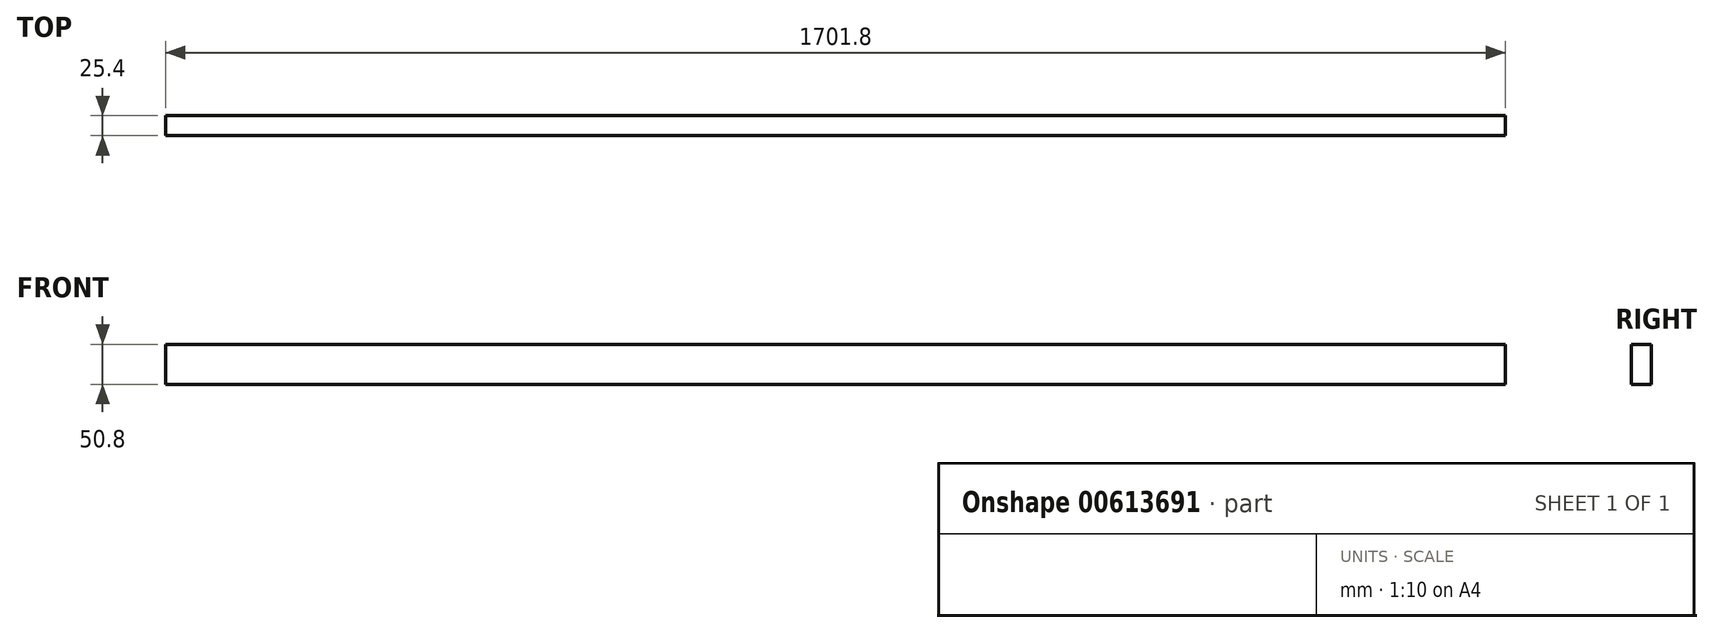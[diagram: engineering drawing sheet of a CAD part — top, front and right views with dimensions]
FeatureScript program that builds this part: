
annotation { "Feature Type Name" : "Feature", "Feature Type Description" : "" }
export const myFeature = defineFeature(function(context is Context, id is Id, definition is map)
    precondition{}
    {
        {
            var Q0;
            Q0=qCreatedBy(makeId("Front.planeOp"),FACE);
            var sketch = newSketch(context, id + "F0", { "sketchPlane" : qUnion([Q0])});
            skLineSegment(sketch, "E0.bottom", {"start": v(-856.45, -131.43) * mm, "end": v(845.35, -131.43) * mm});
            skLineSegment(sketch, "E0.top", {"start": v(-856.45, -182.23) * mm, "end": v(845.35, -182.23) * mm});
            skLineSegment(sketch, "E0.left", {"start": v(-856.45, -131.43) * mm, "end": v(-856.45, -182.23) * mm});
            skLineSegment(sketch, "E0.right", {"start": v(845.35, -131.43) * mm, "end": v(845.35, -182.23) * mm});
            skSolve(sketch);
        }
        {
            var Q0;
            Q0 = qSketchRegion(id + "F0", true);
            extrude(context, id + "F1", {"entities" : qUnion([Q0]), "depth" : 25.4 * mm, "offsetDistance" : 25.4 * mm});
        }
    });
